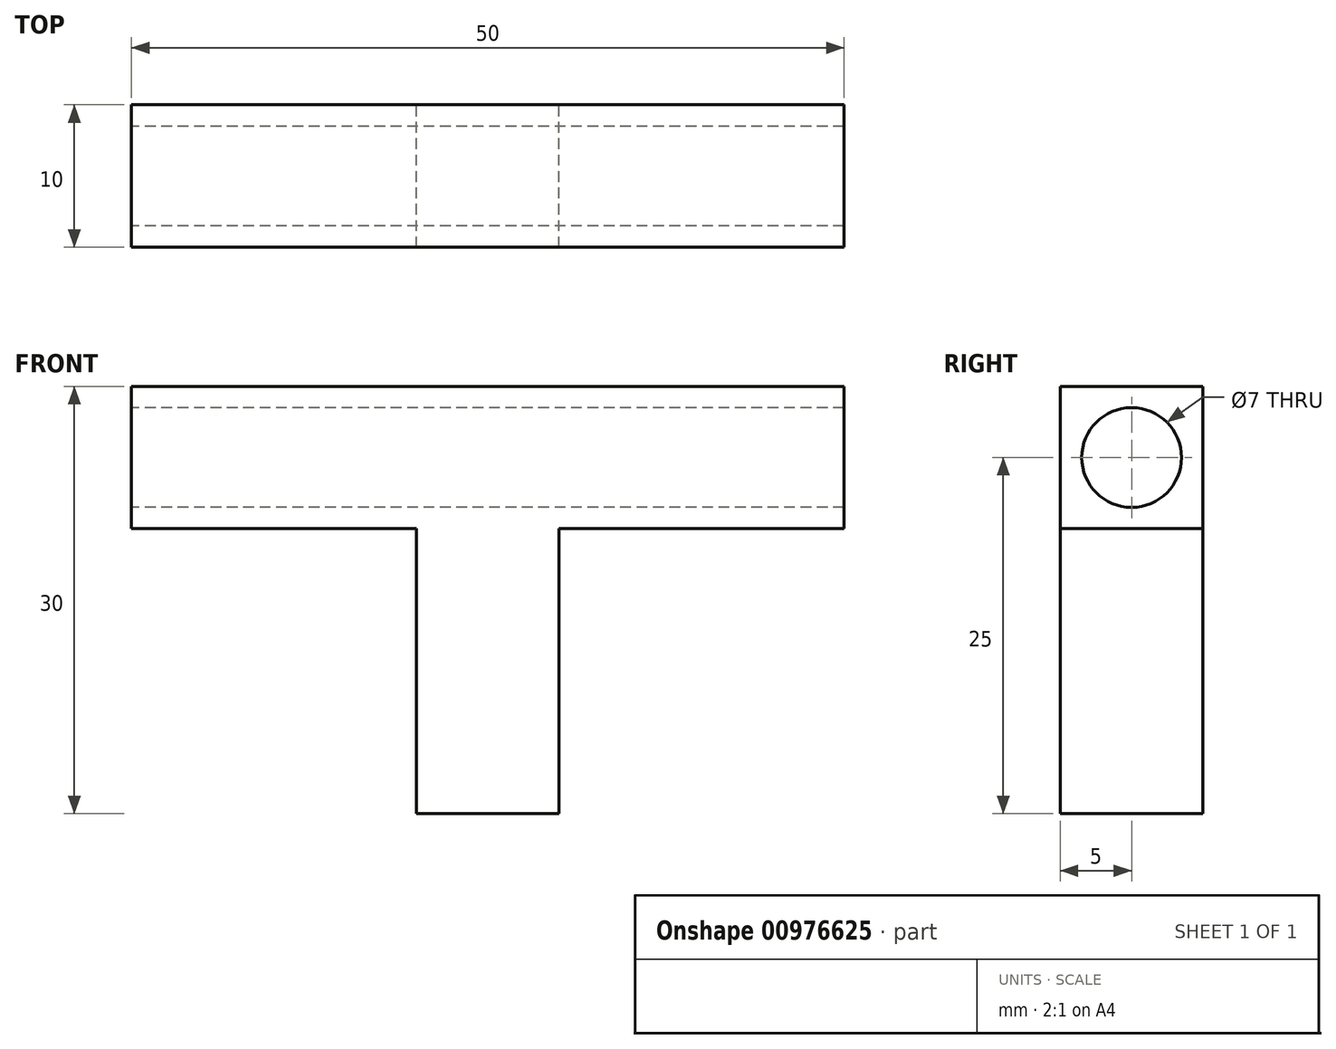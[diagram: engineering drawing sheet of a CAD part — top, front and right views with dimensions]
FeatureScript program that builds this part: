
annotation { "Feature Type Name" : "Feature", "Feature Type Description" : "" }
export const myFeature = defineFeature(function(context is Context, id is Id, definition is map)
    precondition{}
    {
        {
            var Q0;
            Q0=qCreatedBy(makeId("Front.planeOp"),FACE);
            var sketch = newSketch(context, id + "F0", { "sketchPlane" : qUnion([Q0])});
            skPoint(sketch, "E0.top.end.orphan", {"position": v(-8, -50) * mm});
            skPoint(sketch, "E0.top.start.orphan", {"position": v(8, -44) * mm});
            skLineSegment(sketch, "E1.bottom", {"start": v(25, 5) * mm, "end": v(-25, 5) * mm});
            skLineSegment(sketch, "E1.top", {"start": v(25, -5) * mm, "end": v(5, -5) * mm});
            skLineSegment(sketch, "E1.left", {"start": v(25, 5) * mm, "end": v(25, -5) * mm});
            skLineSegment(sketch, "E1.right", {"start": v(-25, 5) * mm, "end": v(-25, -5) * mm});
            skPoint(sketch, "E1.middle", {"position": v(0, 0) * mm});
            skLineSegment(sketch, "E2.top", {"start": v(5, -25) * mm, "end": v(-5, -25) * mm});
            skLineSegment(sketch, "E2.left", {"start": v(5, -5) * mm, "end": v(5, -25) * mm});
            skLineSegment(sketch, "E2.right", {"start": v(-5, -5) * mm, "end": v(-5, -25) * mm});
            skPoint(sketch, "E3.orphan", {"position": v(-5, 25) * mm});
            skPoint(sketch, "E4.orphan", {"position": v(5, 25) * mm});
            skLineSegment(sketch, "E5.trimOffspring", {"start": v(-5, -5) * mm, "end": v(-25, -5) * mm});
            skSolve(sketch);
        }
        {
            var Q0;
            Q0 = qSketchRegion(id + "F0", true);
            extrude(context, id + "F1", {"entities" : qUnion([Q0]), "depth" : 10 * mm, "offsetDistance" : 25 * mm});
        }
        {
            var Q0;
            Q0=makeQuery(id+"F1.opExtrude","SWEPT_FACE",FACE,{"disambiguationData":[OSD([sQuery(id+"F0.wireOp",EDGE,"E1.right")])]});
            var sketch = newSketch(context, id + "F2", { "sketchPlane" : qUnion([Q0])});
            skLineSegment(sketch, "E6", {"start": v(0, -5) * mm, "end": v(5, 0) * mm});
            skCircle(sketch, "E7", {"center": v(5, 0) * mm, "radius": 3.5 * mm});
            skLineSegment(sketch, "E8.trimOffspring", {"start": v(7.47, 2.47) * mm, "end": v(10, 5) * mm});
            skSolve(sketch);
        }
        {
            var Q0;
            Q0 = qSketchRegion(id + "F2", true);
            extrude(context, id + "F3", {"entities" : qUnion([Q0]), "operationType" : NewBodyOperationType.REMOVE, "endBound" : BoundingType.THROUGH_ALL, "oppositeDirection" : true, "depth" : 25 * mm, "offsetDistance" : 25 * mm});
        }
    });
